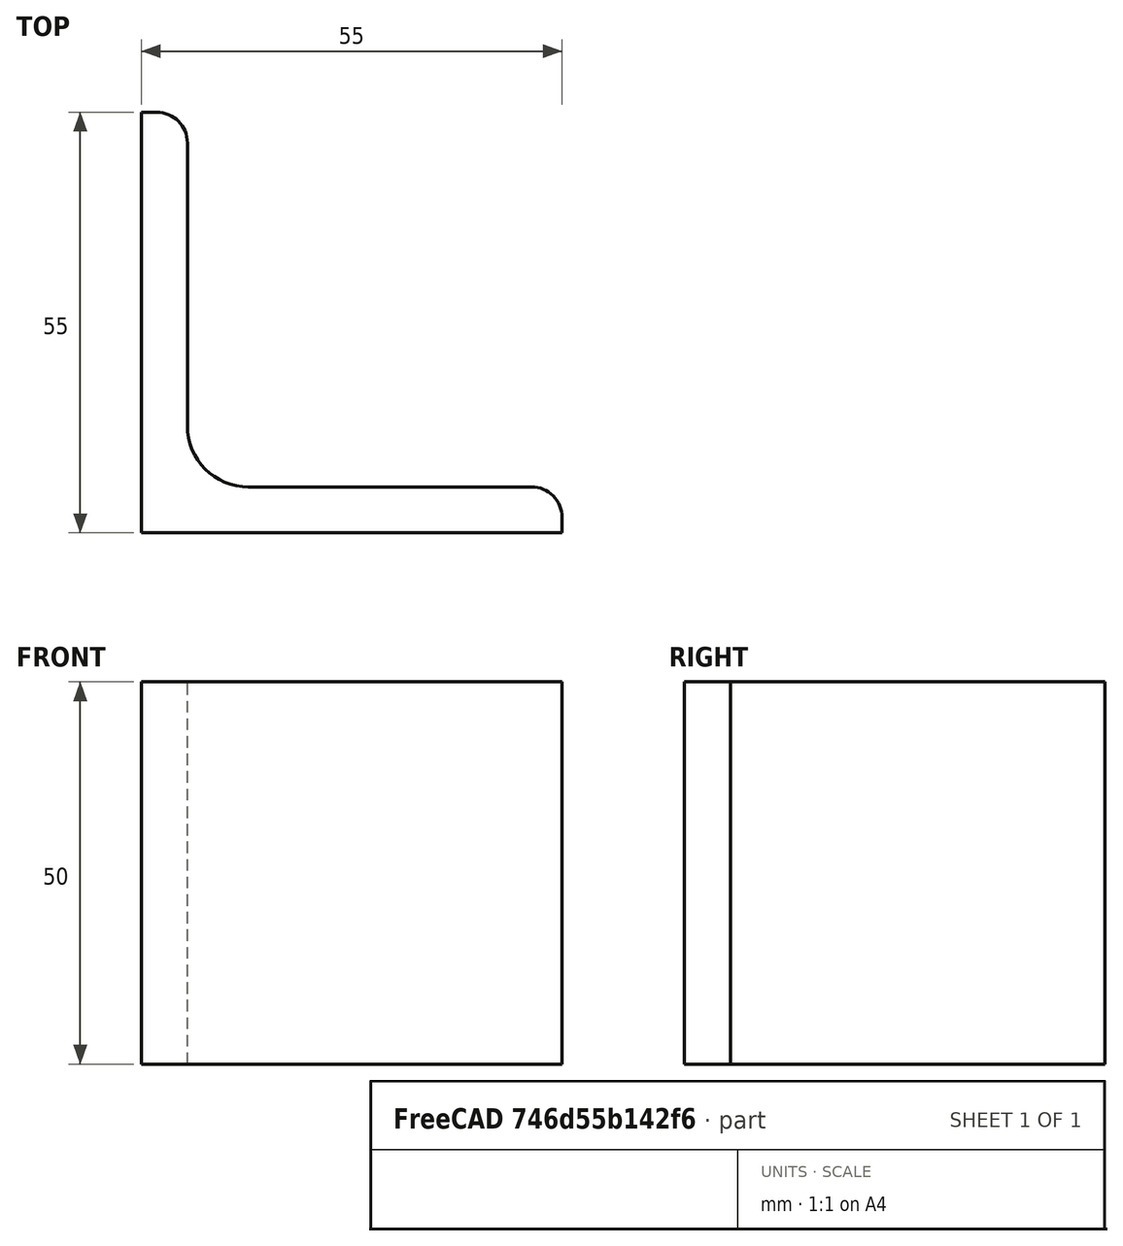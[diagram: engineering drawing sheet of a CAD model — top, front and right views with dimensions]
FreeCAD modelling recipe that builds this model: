
FCSTD DOCUMENT  (FreeCAD 0.15R4671 (Git))
Label: Angle Bar L55x55x6 EN10056 S235JR
License: All rights reserved
LicenseURL: http://en.wikipedia.org/wiki/All_rights_reserved
objects: Sketcher::SketchObject×1, Part::Extrusion×1
note: 2 computed .brp shape members not serialized (recipe doc carries the construction recipe); baked Part::Feature solids carry a one-line shape summary decoded from their .brp

FEATURE [Sketcher::SketchObject] Sketch
  sketch-geometry (9):
    g0: LineSegment StartX=0 StartY=0 StartZ=0 EndX=55 EndY=0 EndZ=0
    g1: LineSegment StartX=55 StartY=0 StartZ=0 EndX=55 EndY=2 EndZ=0
    g2: LineSegment StartX=51 StartY=6 StartZ=0 EndX=14 EndY=6 EndZ=0
    g3: LineSegment StartX=0 StartY=0 StartZ=0 EndX=0 EndY=55 EndZ=0
    g4: LineSegment StartX=0 StartY=55 StartZ=0 EndX=2 EndY=55 EndZ=0
    g5: LineSegment StartX=6 StartY=51 StartZ=0 EndX=6 EndY=14 EndZ=0
    g6: ArcOfCircle CenterX=14 CenterY=14 CenterZ=0 NormalX=0 NormalY=0 NormalZ=1 Radius=8 StartAngle=3.14159 EndAngle=4.71239
    g7: ArcOfCircle CenterX=2 CenterY=51 CenterZ=0 NormalX=0 NormalY=0 NormalZ=1 Radius=4 StartAngle=0 EndAngle=1.5708
    g8: ArcOfCircle CenterX=51 CenterY=2 CenterZ=0 NormalX=0 NormalY=0 NormalZ=1 Radius=4 StartAngle=0 EndAngle=1.5708
  constraints (23):
    c: Coincident(g0,g-1)
    c: Horizontal(g0)
    c: Coincident(g1,g0)
    c: Vertical(g1)
    c: Horizontal(g2)
    c: Coincident(g3,g-1)
    c: Vertical(g3)
    c: Coincident(g4,g3)
    c: Horizontal(g4)
    c: Vertical(g5)
    c: Tangent(g5,g6) = -1.5708
    c: Tangent(g2,g6) = 1.5708
    c: Tangent(g4,g7) = 1.5708
    c: Tangent(g5,g7) = 1.5708
    c: Tangent(g2,g8) = -1.5708
    c: Tangent(g1,g8) = -1.5708
    c: DistanceX(g0) = 55
    c: DistanceY(g3) = 55
    c: DistanceY(g0,g2) = 6
    c: DistanceX(g3,g5) = 6
    c: Radius(g6) = 8
    c: Radius(g8) = 4
    c: Radius(g7) = 4
FEATURE [Part::Extrusion] Extrude  label="Angle Bar L55x55x6 EN10056 S235JR"
  Base = -> Sketch
  Dir = (0,0,50)
  Solid = true
